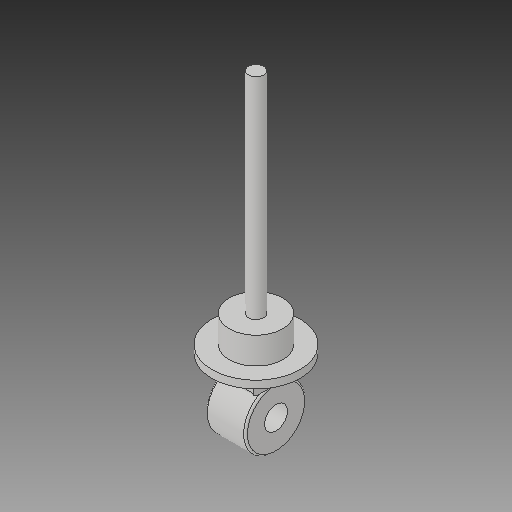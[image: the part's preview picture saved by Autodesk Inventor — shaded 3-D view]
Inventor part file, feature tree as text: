
AUTODESK INVENTOR PART (.ipt)
format: ipt  version: 2018 (Build 220112000, 112)  size: 164,864 bytes
history: native  units: mm
features: sketch x5, extrude x4, fillet x4, other x2, hole x1
ambient origin geometry x8: Origin, YZ Plane, XZ Plane, XY Plane, X Axis, Y Axis, Z Axis, Center Point
bodies: Body1 (feature_tree)
feature tree (16):
  other  "ソリッド1"
  extrude  "押し出し1"  Depth=32.0mm
  hole  "穴1"  [1 undecoded]
  other  "作業平面1"
  extrude  "押し出し2"  Depth=24.0mm
  extrude  "押し出し3"  Depth=46.0mm
  extrude  "押し出し4"  Depth=4.0mm TaperAngle=0.0deg
  fillet  "フィレット1"  Radius=28.0mm
  fillet  "フィレット2"  Radius=14.0mm
  fillet  "フィレット3"  Radius=8.0mm
  fillet  "フィレット4"  Radius=110.0mm
  sketch  "スケッチ1"
  sketch  "スケッチ2"
  sketch  "スケッチ4"
  sketch  "スケッチ5"
  sketch  "スケッチ6"
note: 1 required parameter value undecoded (feature->parameter linkage not recoverable at this tier; creation-order binding heuristic only, values carry confidence <= 0.55)
